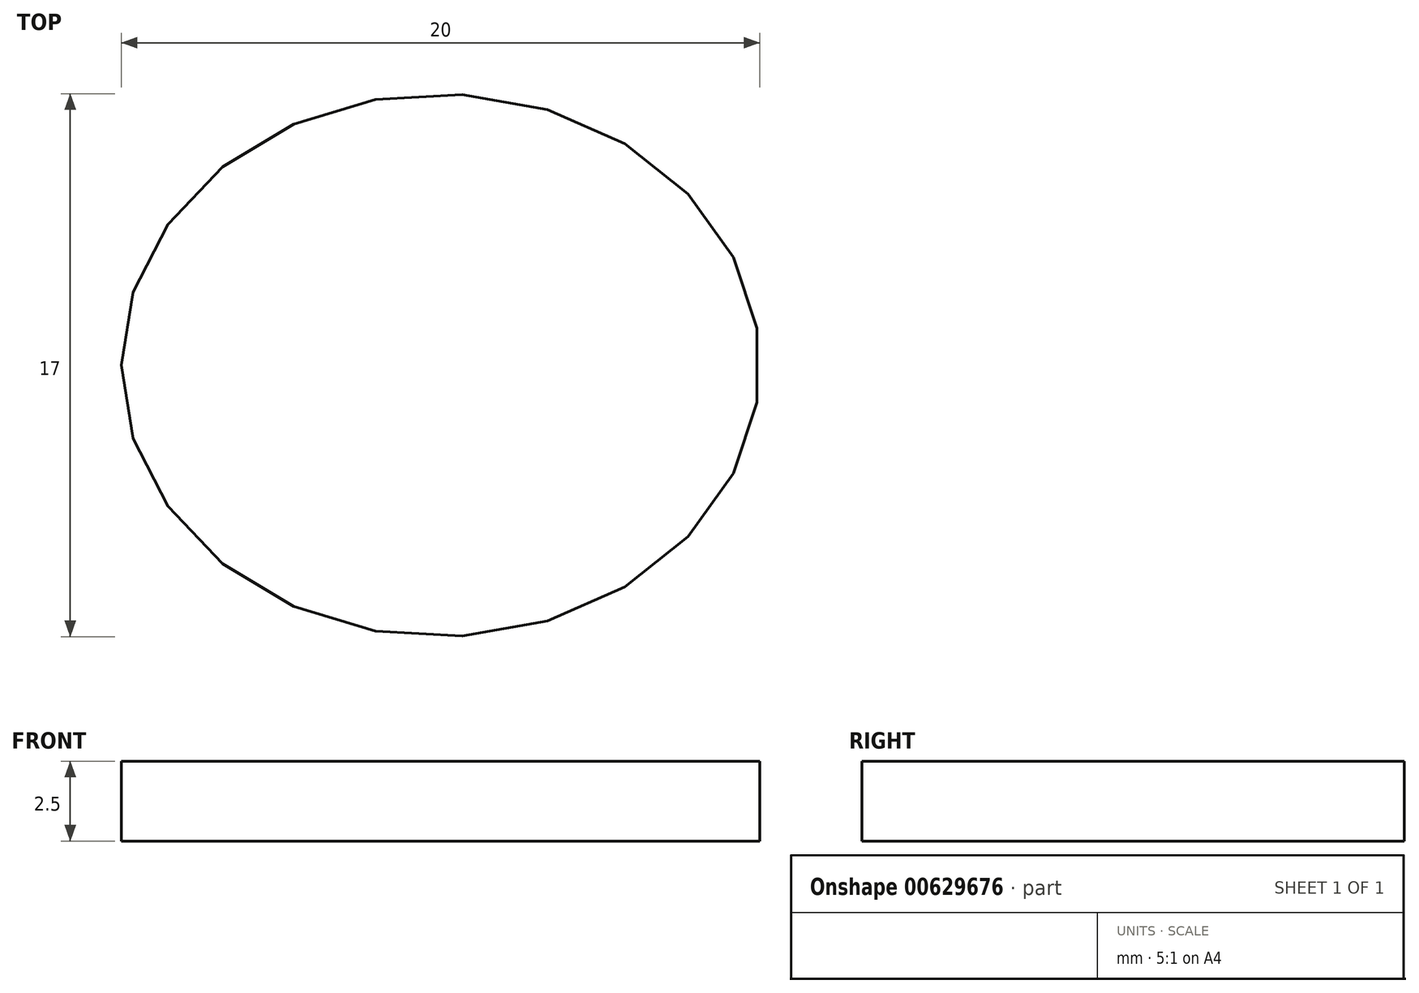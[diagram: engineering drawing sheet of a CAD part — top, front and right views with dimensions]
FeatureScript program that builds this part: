
annotation { "Feature Type Name" : "Feature", "Feature Type Description" : "" }
export const myFeature = defineFeature(function(context is Context, id is Id, definition is map)
    precondition{}
    {
        {
            var Q0;
            Q0=qCreatedBy(makeId("Top.planeOp"),FACE);
            var sketch = newSketch(context, id + "F0", { "sketchPlane" : qUnion([Q0])});
            skEllipse(sketch, "E0", {"center": v(0, 0) * mm, "majorRadius": 10 * mm, "minorRadius": 8.5 * mm, "majorAxis": v(-1, 0)});
            skFitSpline(sketch, "E1.0", {"points": [v(-11.96, 1.07) * mm, v(-12.02, 0) * mm, v(-11.96, -1.07) * mm, v(-11.71, -2.47) * mm, v(-11.23, -3.82) * mm, v(-10.53, -5.08) * mm, v(-9.7, -6.27) * mm, v(-8.42, -7.58) * mm, v(-6.9, -8.65) * mm, v(-5.55, -9.33) * mm, v(-4.14, -9.9) * mm, v(-2.67, -10.28) * mm, v(-1.15, -10.47) * mm, v(0, -10.52) * mm, v(1.15, -10.47) * mm, v(2.67, -10.28) * mm, v(4.14, -9.9) * mm, v(5.55, -9.33) * mm, v(6.9, -8.65) * mm, v(8.42, -7.58) * mm, v(9.7, -6.27) * mm, v(10.53, -5.08) * mm, v(11.23, -3.82) * mm, v(11.71, -2.47) * mm, v(11.96, -1.07) * mm, v(12.02, 0) * mm, v(11.96, 1.07) * mm, v(11.71, 2.47) * mm, v(11.23, 3.82) * mm, v(10.53, 5.08) * mm, v(9.7, 6.27) * mm, v(8.42, 7.58) * mm, v(6.9, 8.65) * mm, v(5.55, 9.33) * mm, v(4.14, 9.9) * mm, v(2.67, 10.28) * mm, v(1.15, 10.47) * mm, v(0, 10.52) * mm, v(-1.15, 10.47) * mm, v(-2.67, 10.28) * mm, v(-4.14, 9.9) * mm, v(-5.55, 9.33) * mm, v(-6.9, 8.65) * mm, v(-8.42, 7.58) * mm, v(-9.7, 6.27) * mm, v(-10.53, 5.08) * mm, v(-11.23, 3.82) * mm, v(-11.71, 2.47) * mm, v(-11.96, 1.07) * mm, v(-12.02, 0) * mm, v(-11.96, -1.07) * mm, v(-11.96, 1.07) * mm]});
            skSolve(sketch);
        }
        {
            var Q0;
            Q0=qSketchRegion(id+"F0",true);
            extrude(context, id + "F1", {"entities" : qUnion([Q0]), "depth" : 2.5 * mm, "offsetDistance" : 25 * mm});
        }
    });
